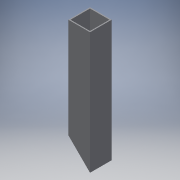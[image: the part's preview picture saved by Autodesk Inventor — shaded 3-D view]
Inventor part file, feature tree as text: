
AUTODESK INVENTOR PART (.ipt)
format: ipt  version: 2018 (Build 220112000, 112)  size: 104,960 bytes
history: native  units: mm
features: other x1, extrude x1, chamfer x1, sketch x1
ambient origin geometry x8: Origin, YZ Plane, XZ Plane, XY Plane, X Axis, Y Axis, Z Axis, Center Point
bodies: Body1 (feature_tree)
feature tree (4):
  other  "ソリッド1"
  extrude  "押し出し1"  Depth=32.0mm
  chamfer  "面取り1"  Distance=32.0mm
  sketch  "スケッチ1"
